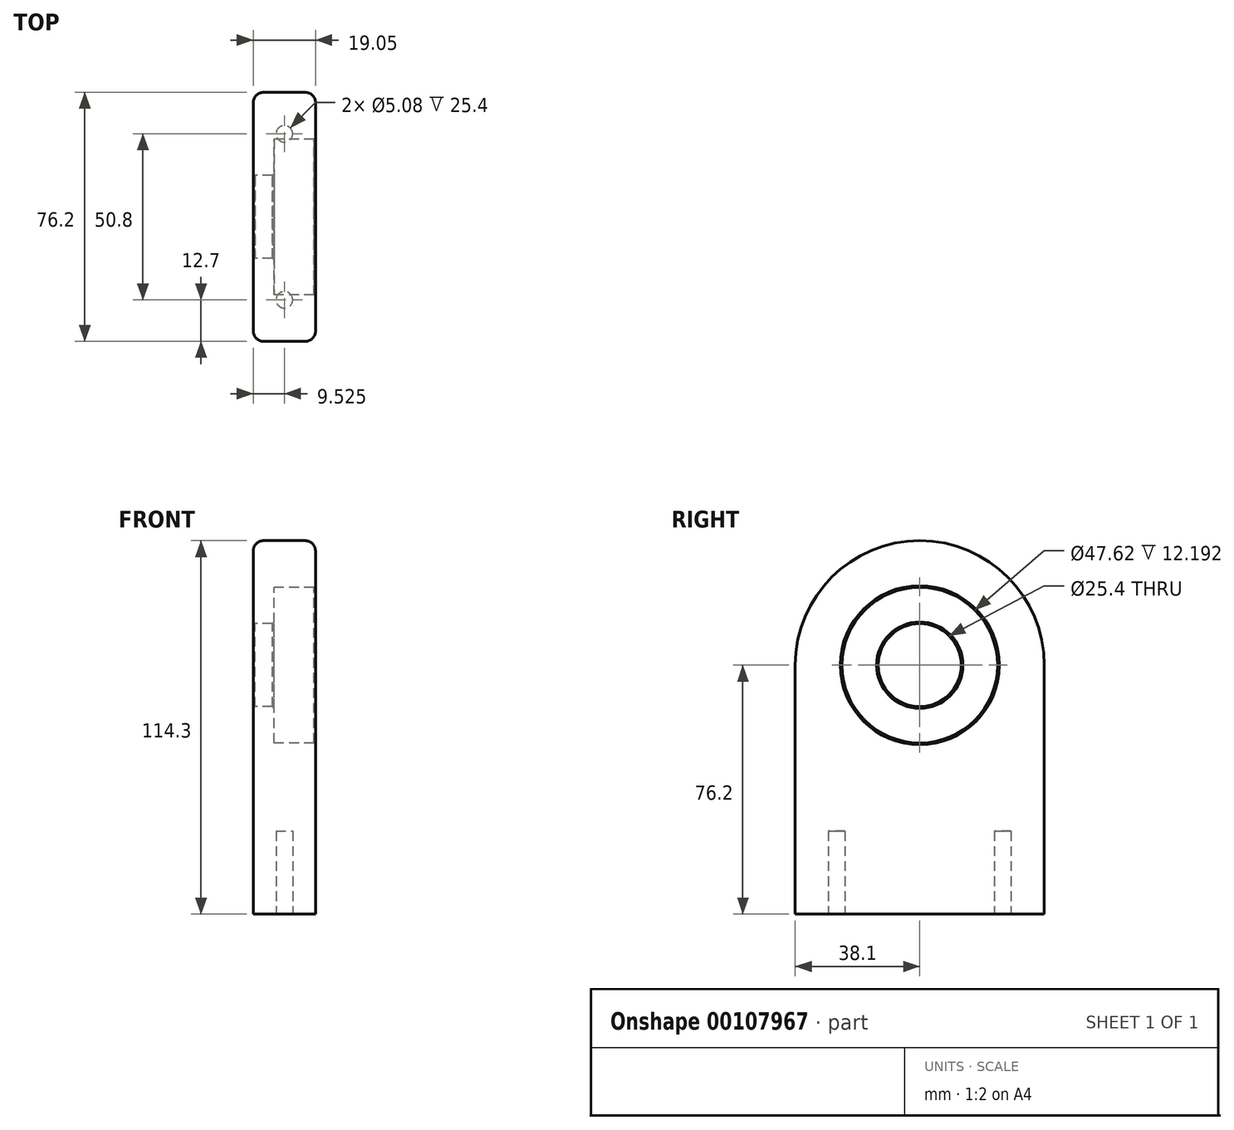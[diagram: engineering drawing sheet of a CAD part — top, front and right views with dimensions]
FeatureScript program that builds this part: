
annotation { "Feature Type Name" : "Feature", "Feature Type Description" : "" }
export const myFeature = defineFeature(function(context is Context, id is Id, definition is map)
    precondition{}
    {
        {
            var Q0;
            Q0=qCreatedBy(makeId("Right.planeOp"),FACE);
            var sketch = newSketch(context, id + "F0", { "sketchPlane" : qUnion([Q0])});
            skCircle(sketch, "E0", {"center": v(0, 0) * mm, "radius": 23.81 * mm});
            skLineSegment(sketch, "E1.bottom", {"start": v(38.1, -76.2) * mm, "end": v(-38.1, -76.2) * mm});
            skLineSegment(sketch, "E1.left", {"start": v(38.1, -76.2) * mm, "end": v(38.1, 0) * mm});
            skLineSegment(sketch, "E1.right", {"start": v(-38.1, -76.2) * mm, "end": v(-38.1, 0) * mm});
            skArc(sketch, "E2", {"start": v(38.1, 0) * mm, "mid": v(0, 38.1) * mm, "end": v(-38.1, 0) * mm});
            skCircle(sketch, "E3", {"center": v(0, 0) * mm, "radius": 12.7 * mm});
            skSolve(sketch);
        }
        {
            var Q0;
            Q0=makeQuery(id+"F0.imprint","IMPRINT",FACE,{"disambiguationData":[TD([[makeQuery(id+"F0.imprint","IMPRINT",EDGE,{"derivedFrom":sQuery(id+"F0.wireOp",EDGE,"E0")}),-1.0]])]});
            extrude(context, id + "F1", {"entities" : qUnion([Q0]), "depth" : 19.05 * mm});
        }
        {
            var Q0;
            Q0=makeQuery(id+"F0.imprint","IMPRINT",FACE,{"disambiguationData":[TD([[makeQuery(id+"F0.imprint","IMPRINT",EDGE,{"derivedFrom":sQuery(id+"F0.wireOp",EDGE,"E0")}),1.0]])]});
            extrude(context, id + "F2", {"entities" : qUnion([Q0]), "operationType" : NewBodyOperationType.ADD, "depth" : 6.35 * mm});
        }
        {
            var Q0;
            Q0=makeQuery(id+"F2.opExtrude","CAP_EDGE",EDGE,{"disambiguationData":[OSD([sQuery(id+"F0.wireOp",EDGE,"E3")])],"isStart":true});
            var Q1;
            Q1=makeQuery(id+"F1.opExtrude","CAP_EDGE",EDGE,{"disambiguationData":[OSD([sQuery(id+"F0.wireOp",EDGE,"E0")])],"isStart":false});
            var Q2;
            Q2=makeQuery(id+"F2.opExtrude","CAP_EDGE",EDGE,{"disambiguationData":[OSD([sQuery(id+"F0.wireOp",EDGE,"E3")])],"isStart":false});
            chamfer(context, id + "F3", {"entities" : qUnion([Q0, Q1, Q2]), "width" : 0.5 * mm, "tangentPropagation" : true});
        }
        {
            var Q0;
            Q0=makeQuery(id+"F1.opExtrude","SWEPT_FACE",FACE,{"disambiguationData":[OSD([sQuery(id+"F0.wireOp",EDGE,"E1.bottom")])]});
            var sketch = newSketch(context, id + "F4", { "sketchPlane" : qUnion([Q0])});
            skLineSegment(sketch, "E4", {"start": v(9.53, 38.1) * mm, "end": v(9.53, -37.6) * mm, "construction": true});
            skCircle(sketch, "E5", {"center": v(9.53, 25.4) * mm, "radius": 2.54 * mm});
            skCircle(sketch, "E6", {"center": v(9.53, -25.4) * mm, "radius": 2.54 * mm});
            skSolve(sketch);
        }
        {
            var Q0;
            Q0=makeQuery(id+"F4.imprint","IMPRINT",FACE,{"disambiguationData":[TD([[makeQuery(id+"F4.imprint","IMPRINT",EDGE,{"derivedFrom":sQuery(id+"F4.wireOp",EDGE,"E5")}),1.0]])]});
            var Q1;
            Q1=makeQuery(id+"F4.imprint","IMPRINT",FACE,{"disambiguationData":[TD([[makeQuery(id+"F4.imprint","IMPRINT",EDGE,{"derivedFrom":sQuery(id+"F4.wireOp",EDGE,"E6")}),1.0]])]});
            extrude(context, id + "F5", {"entities" : qUnion([Q0, Q1]), "operationType" : NewBodyOperationType.REMOVE, "oppositeDirection" : true, "depth" : 25.4 * mm});
        }
        {
            var Q0;
            Q0=makeQuery(id+"F1.opExtrude","CAP_EDGE",EDGE,{"disambiguationData":[OSD([sQuery(id+"F0.wireOp",EDGE,"E1.right")])],"isStart":false});
            var Q1;
            Q1=makeQuery(id+"F1.opExtrude","CAP_EDGE",EDGE,{"disambiguationData":[OSD([sQuery(id+"F0.wireOp",EDGE,"E1.right")])],"isStart":true});
            fillet(context, id + "F6", {"entities" : qUnion([Q0, Q1]), "radius" : 3.17 * mm, "tangentPropagation" : true, "allowEdgeOverflow" : false});
        }
    });
